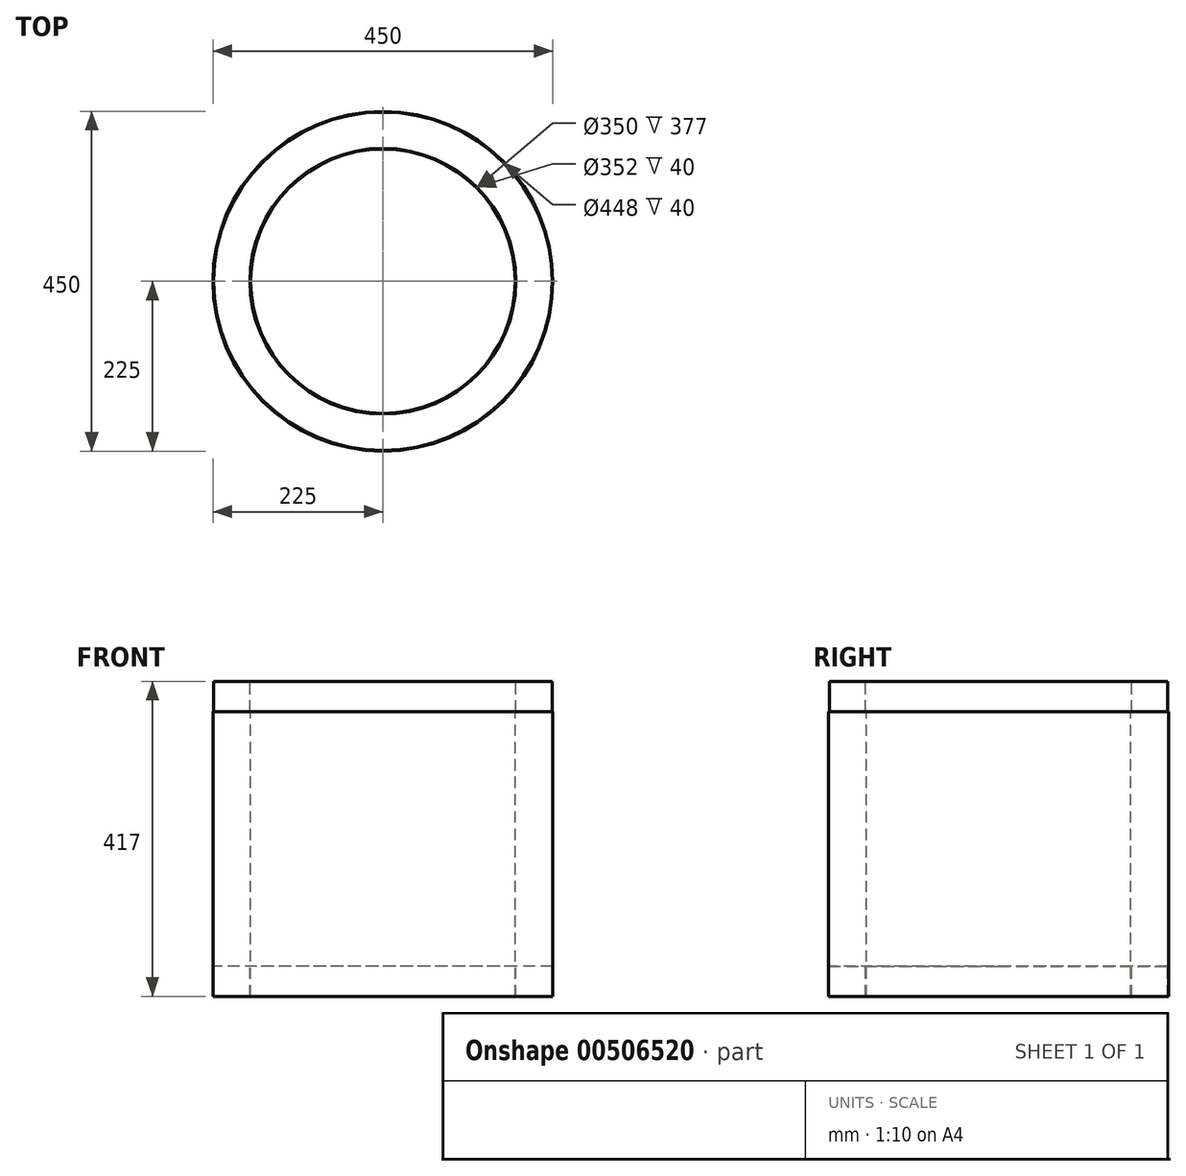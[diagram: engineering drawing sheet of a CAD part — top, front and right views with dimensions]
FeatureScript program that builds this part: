
annotation { "Feature Type Name" : "Feature", "Feature Type Description" : "" }
export const myFeature = defineFeature(function(context is Context, id is Id, definition is map)
    precondition{}
    {
        {
            var Q0;
            Q0=qCreatedBy(makeId("Front.planeOp"),FACE);
            var sketch = newSketch(context, id + "F0", { "sketchPlane" : qUnion([Q0])});
            skLineSegment(sketch, "E0", {"start": v(0, 74.87) * mm, "end": v(0, -73.71) * mm, "construction": true});
            skLineSegment(sketch, "E1", {"start": v(0, 374.84) * mm, "end": v(0, -528.94) * mm, "construction": true});
            skLineSegment(sketch, "E2", {"start": v(-175, -489.75) * mm, "end": v(-175, -112.75) * mm});
            skLineSegment(sketch, "E3", {"start": v(-175, -112.75) * mm, "end": v(-176, -112.75) * mm});
            skLineSegment(sketch, "E4", {"start": v(-176, -112.75) * mm, "end": v(-176, -72.75) * mm});
            skLineSegment(sketch, "E5", {"start": v(-176, -72.75) * mm, "end": v(-224, -72.75) * mm});
            skLineSegment(sketch, "E6", {"start": v(-224, -72.75) * mm, "end": v(-224, -112.75) * mm});
            skLineSegment(sketch, "E7", {"start": v(-224, -112.75) * mm, "end": v(-225, -112.75) * mm});
            skLineSegment(sketch, "E8", {"start": v(-225, -112.75) * mm, "end": v(-225, -489.75) * mm});
            skLineSegment(sketch, "E9", {"start": v(-225, -489.75) * mm, "end": v(-224, -489.75) * mm});
            skLineSegment(sketch, "E10", {"start": v(-224, -489.75) * mm, "end": v(-224, -449.75) * mm});
            skLineSegment(sketch, "E11", {"start": v(-224, -449.75) * mm, "end": v(-176, -449.75) * mm});
            skLineSegment(sketch, "E12", {"start": v(-176, -449.75) * mm, "end": v(-176, -489.75) * mm});
            skLineSegment(sketch, "E13", {"start": v(-176, -489.75) * mm, "end": v(-175, -489.75) * mm});
            skSolve(sketch);
        }
        {
            var Q0;
            Q0=qSketchRegion(id+"F0",true);
            var Q1;
            Q1=sQuery(id+"F0.wireOp",EDGE,"E1");
            revolve(context, id + "F1", {"entities" : qUnion([Q0]), "axis" : qUnion([Q1]), "revolveType" : RevolveType.FULL});
        }
    });
